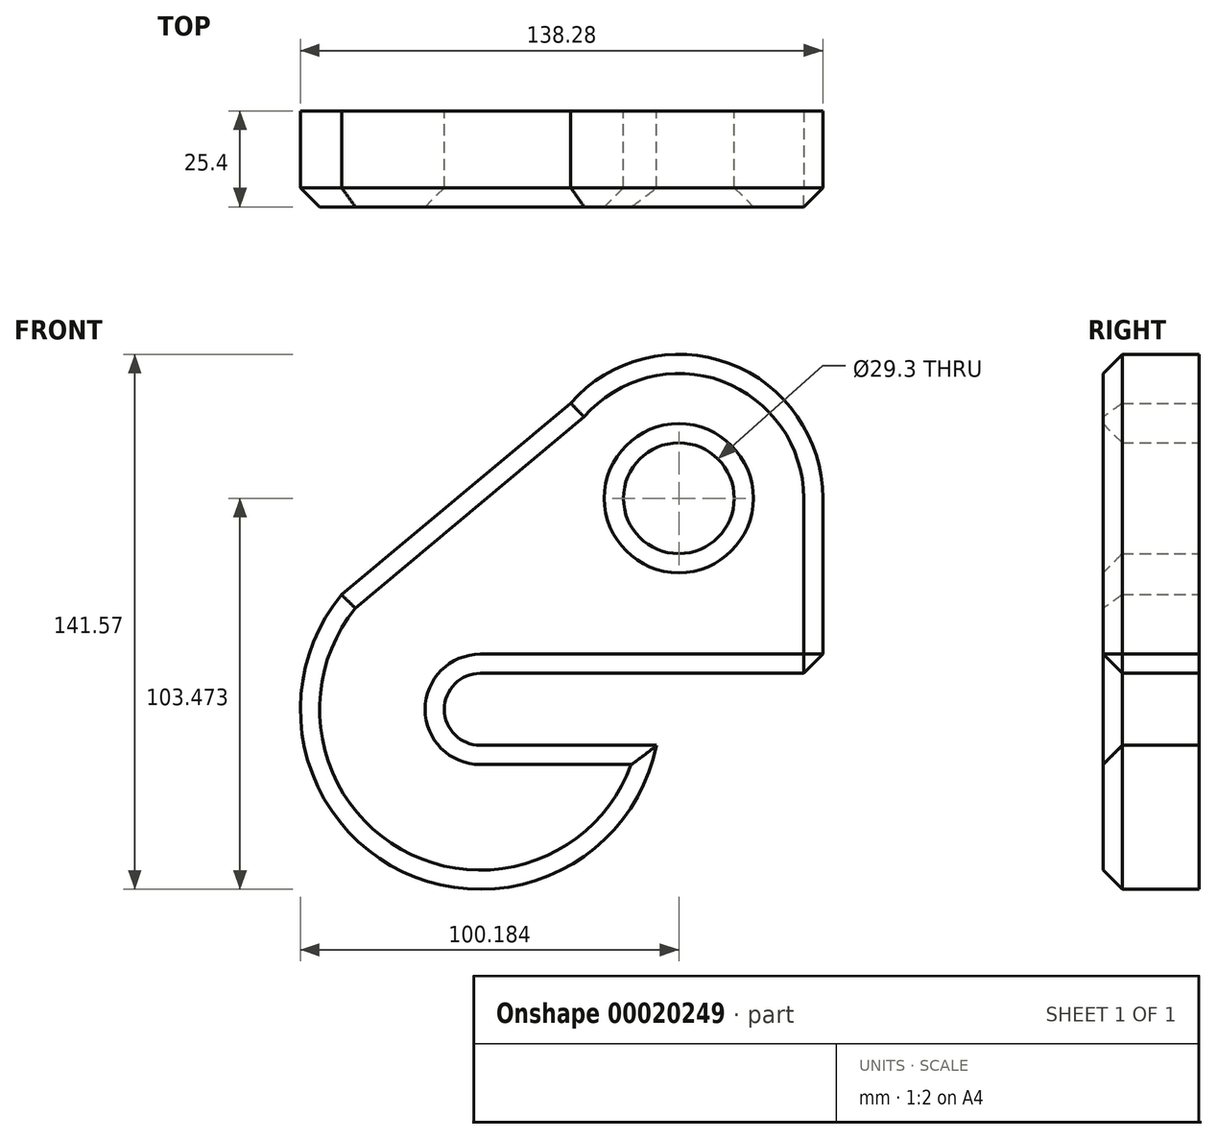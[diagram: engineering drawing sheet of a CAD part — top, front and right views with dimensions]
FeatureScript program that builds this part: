
annotation { "Feature Type Name" : "Feature", "Feature Type Description" : "" }
export const myFeature = defineFeature(function(context is Context, id is Id, definition is map)
    precondition{}
    {
        {
            var Q0;
            Q0=qCreatedBy(makeId("Front.planeOp"),FACE);
            var sketch = newSketch(context, id + "F0", { "sketchPlane" : qUnion([Q0])});
            skArc(sketch, "E0", {"start": v(0, 9.53) * mm, "mid": v(-9.53, 0) * mm, "end": v(0, -9.53) * mm});
            skLineSegment(sketch, "E1", {"start": v(0, -9.53) * mm, "end": v(46.66, -9.53) * mm});
            skArc(sketch, "E2.trimOffspring", {"start": v(90.65, 55.84) * mm, "mid": v(65.99, 91.5) * mm, "end": v(23.92, 80.98) * mm});
            skArc(sketch, "E3.trimOffspring", {"start": v(-36.71, 30.34) * mm, "mid": v(-20.54, -42.97) * mm, "end": v(46.66, -9.53) * mm});
            skLineSegment(sketch, "E4", {"start": v(90.65, 55.84) * mm, "end": v(90.65, 9.52) * mm});
            skCircle(sketch, "E5", {"center": v(52.55, 55.84) * mm, "radius": 14.65 * mm});
            skLineSegment(sketch, "E6", {"start": v(23.92, 80.98) * mm, "end": v(-36.71, 30.34) * mm});
            skPoint(sketch, "E7.end.orphan", {"position": v(82.22, 9.53) * mm});
            skLineSegment(sketch, "E8", {"start": v(0, 9.53) * mm, "end": v(90.65, 9.52) * mm});
            skSolve(sketch);
        }
        {
            var Q0;
            Q0=makeQuery(id+"F0.imprint","IMPRINT",FACE,{"disambiguationData":[TD([[makeQuery(id+"F0.imprint","IMPRINT",EDGE,{"derivedFrom":sQuery(id+"F0.wireOp",EDGE,"E0")}),-1.0]])]});
            extrude(context, id + "F1", {"entities" : qUnion([Q0]), "depth" : 25.4 * mm});
        }
        {
            var Q0;
            Q0=makeQuery(id+"F1.opExtrude","CAP_EDGE",EDGE,{"disambiguationData":[OSD([sQuery(id+"F0.wireOp",EDGE,"E4")])],"isStart":false});
            var Q1;
            Q1=makeQuery(id+"F1.opExtrude","CAP_EDGE",EDGE,{"disambiguationData":[OSD([sQuery(id+"F0.wireOp",EDGE,"E2.trimOffspring")])],"isStart":false});
            var Q2;
            Q2=makeQuery(id+"F1.opExtrude","CAP_EDGE",EDGE,{"disambiguationData":[OSD([sQuery(id+"F0.wireOp",EDGE,"E6")])],"isStart":false});
            var Q3;
            Q3=makeQuery(id+"F1.opExtrude","CAP_EDGE",EDGE,{"disambiguationData":[OSD([sQuery(id+"F0.wireOp",EDGE,"E5")])],"isStart":false});
            var Q4;
            Q4=makeQuery(id+"F1.opExtrude","CAP_EDGE",EDGE,{"disambiguationData":[OSD([sQuery(id+"F0.wireOp",EDGE,"E3.trimOffspring")])],"isStart":false});
            var Q5;
            Q5=makeQuery(id+"F1.opExtrude","CAP_EDGE",EDGE,{"disambiguationData":[OSD([sQuery(id+"F0.wireOp",EDGE,"E1")])],"isStart":false});
            var Q6;
            Q6=makeQuery(id+"F1.opExtrude","CAP_EDGE",EDGE,{"disambiguationData":[OSD([sQuery(id+"F0.wireOp",EDGE,"E8")])],"isStart":false});
            var Q7;
            Q7=makeQuery(id+"F1.opExtrude","CAP_EDGE",EDGE,{"disambiguationData":[OSD([sQuery(id+"F0.wireOp",EDGE,"E0")])],"isStart":false});
            var Q8;
            Q8=makeQuery(id+"F1.opExtrude","SWEPT_EDGE",EDGE,{"disambiguationData":[OSD([sQuery(id+"F0.wireOp",EDGE,"E4"),sQuery(id+"F0.wireOp",EDGE,"E8")])]});
            chamfer(context, id + "F2", {"entities" : qUnion([Q0, Q1, Q2, Q3, Q4, Q5, Q6, Q7, Q8]), "width" : 5.08 * mm, "tangentPropagation" : true});
        }
    });
